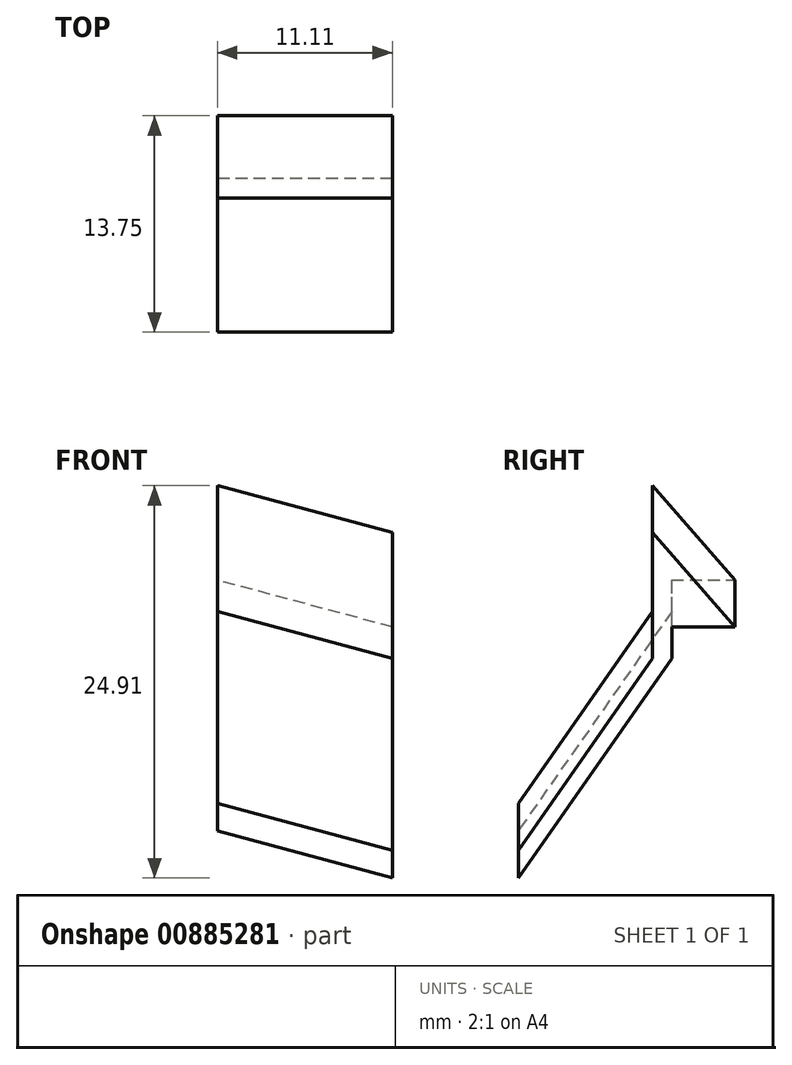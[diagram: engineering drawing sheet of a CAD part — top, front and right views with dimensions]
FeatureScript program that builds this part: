
annotation { "Feature Type Name" : "Feature", "Feature Type Description" : "" }
export const myFeature = defineFeature(function(context is Context, id is Id, definition is map)
    precondition{}
    {
        {
            var Q0;
            Q0=qCreatedBy(makeId("Right.planeOp"),FACE);
            var sketch = newSketch(context, id + "F0", { "sketchPlane" : qUnion([Q0])});
            skLineSegment(sketch, "E0", {"start": v(0, 0) * mm, "end": v(0, -15) * mm, "construction": true});
            skLineSegment(sketch, "E1", {"start": v(0, 0) * mm, "end": v(-9.75, -13.93) * mm});
            skLineSegment(sketch, "E2", {"start": v(-9.75, -13.93) * mm, "end": v(-9.75, -12.18) * mm});
            skLineSegment(sketch, "E3", {"start": v(-9.75, -12.18) * mm, "end": v(-1.22, 0) * mm});
            skLineSegment(sketch, "E4", {"start": v(0, 0) * mm, "end": v(0, 2) * mm});
            skLineSegment(sketch, "E5", {"start": v(0, 2) * mm, "end": v(4, 2) * mm});
            skLineSegment(sketch, "E6", {"start": v(-1.22, 8) * mm, "end": v(4, 2) * mm});
            skLineSegment(sketch, "E7", {"start": v(-1.22, 0) * mm, "end": v(-1.22, 2) * mm});
            skLineSegment(sketch, "E8", {"start": v(-1.22, 2) * mm, "end": v(-1.22, 8) * mm});
            skSolve(sketch);
        }
        {
            var Q0;
            Q0=sQuery(id+"F0.wireOp",EDGE,"E8");
            cPlane(context, id + "F1", {"entities" : qUnion([Q0]), "cplaneType" : CPlaneType.LINE_ANGLE, "offset" : 25 * mm, "angle" : 90 * degree, "width" : 150 * mm, "height" : 150 * mm});
        }
        {
            var Q0;
            Q0=qCreatedBy(id+"F1.planeOp",FACE);
            var sketch = newSketch(context, id + "F2", { "sketchPlane" : qUnion([Q0])});
            skPoint(sketch, "E9.0", {"position": v(0, 8) * mm});
            skLineSegment(sketch, "E10.0", {"start": v(0, 2) * mm, "end": v(0, 8) * mm});
            skLineSegment(sketch, "E11", {"start": v(0, 8) * mm, "end": v(11.1, 10.98) * mm});
            skSolve(sketch);
        }
        {
            var Q0;
            Q0=makeQuery(id+"F0.imprint","IMPRINT",FACE,{"disambiguationData":[TD([[makeQuery(id+"F0.imprint","IMPRINT",EDGE,{"derivedFrom":sQuery(id+"F0.wireOp",EDGE,"E1")}),-1.0]])]});
            var Q1;
            Q1=sQuery(id+"F2.wireOp",EDGE,"E11");
            sweep(context, id + "F3", {"profiles" : qUnion([Q0]), "path" : qUnion([Q1])});
        }
    });
